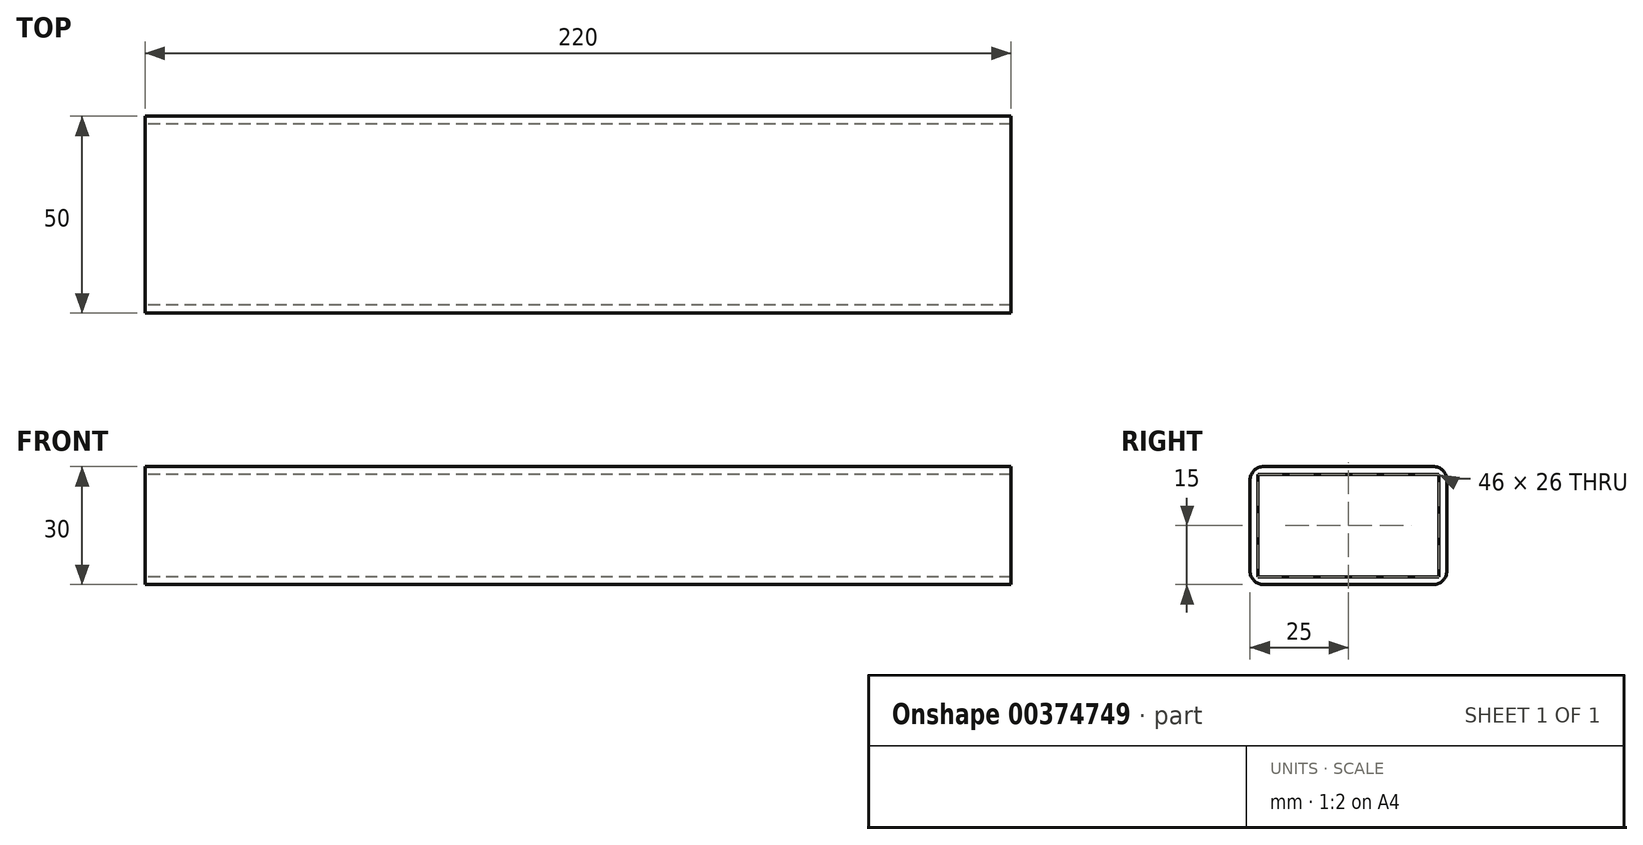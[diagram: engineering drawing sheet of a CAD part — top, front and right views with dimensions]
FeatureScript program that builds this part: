
annotation { "Feature Type Name" : "Feature", "Feature Type Description" : "" }
export const myFeature = defineFeature(function(context is Context, id is Id, definition is map)
    precondition{}
    {
        {
            var Q0;
            Q0=qCreatedBy(makeId("Right.planeOp"),FACE);
            var sketch = newSketch(context, id + "F0", { "sketchPlane" : qUnion([Q0])});
            skLineSegment(sketch, "E0.bottom", {"start": v(21.5, 15) * mm, "end": v(-21.5, 15) * mm});
            skLineSegment(sketch, "E0.top", {"start": v(21.5, -15) * mm, "end": v(-21.5, -15) * mm});
            skLineSegment(sketch, "E0.left", {"start": v(25, 11.5) * mm, "end": v(25, -11.5) * mm});
            skLineSegment(sketch, "E0.right", {"start": v(-25, 11.5) * mm, "end": v(-25, -11.5) * mm});
            skPoint(sketch, "E0.middle", {"position": v(0, 0) * mm});
            skLineSegment(sketch, "E1.bottom", {"start": v(23, 13) * mm, "end": v(-23, 13) * mm});
            skLineSegment(sketch, "E1.top", {"start": v(23, -13) * mm, "end": v(-23, -13) * mm});
            skLineSegment(sketch, "E1.left", {"start": v(23, 13) * mm, "end": v(23, -13) * mm});
            skLineSegment(sketch, "E1.right", {"start": v(-23, 13) * mm, "end": v(-23, -13) * mm});
            skPoint(sketch, "E2.visualSharp", {"position": v(-25, 15) * mm});
            skArc(sketch, "E2.filletArc", {"start": v(-21.5, 15) * mm, "mid": v(-23.97, 13.97) * mm, "end": v(-25, 11.5) * mm});
            skPoint(sketch, "E3.visualSharp", {"position": v(25, 15) * mm});
            skArc(sketch, "E3.filletArc", {"start": v(25, 11.5) * mm, "mid": v(23.97, 13.97) * mm, "end": v(21.5, 15) * mm});
            skPoint(sketch, "E4.visualSharp", {"position": v(25, -15) * mm});
            skArc(sketch, "E4.filletArc", {"start": v(21.5, -15) * mm, "mid": v(23.97, -13.97) * mm, "end": v(25, -11.5) * mm});
            skPoint(sketch, "E5.visualSharp", {"position": v(-25, -15) * mm});
            skArc(sketch, "E5.filletArc", {"start": v(-25, -11.5) * mm, "mid": v(-23.97, -13.97) * mm, "end": v(-21.5, -15) * mm});
            skSolve(sketch);
        }
        {
            var Q0;
            Q0=makeQuery(id+"F0.imprint","IMPRINT",FACE,{"disambiguationData":[TD([[makeQuery(id+"F0.imprint","IMPRINT",EDGE,{"derivedFrom":sQuery(id+"F0.wireOp",EDGE,"E0.bottom")}),1.0]])]});
            extrude(context, id + "F1", {"entities" : qUnion([Q0]), "depth" : 220 * mm});
        }
    });
